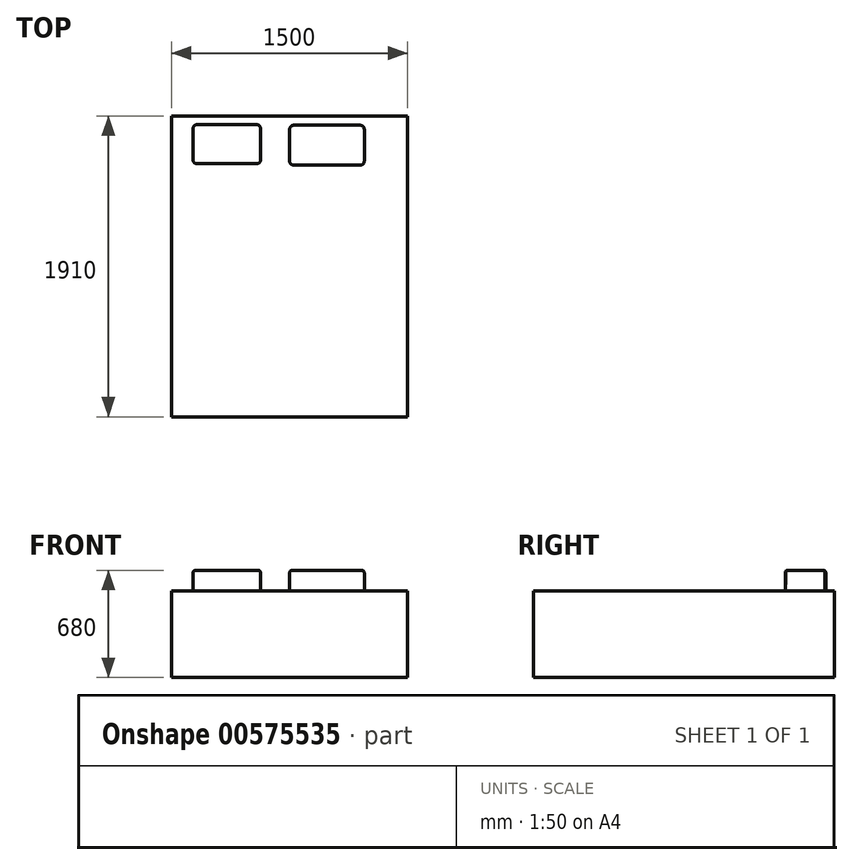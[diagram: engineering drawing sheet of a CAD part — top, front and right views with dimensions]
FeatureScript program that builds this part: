
annotation { "Feature Type Name" : "Feature", "Feature Type Description" : "" }
export const myFeature = defineFeature(function(context is Context, id is Id, definition is map)
    precondition{}
    {
        {
            var Q0;
            Q0=qCreatedBy(makeId("Top.planeOp"),FACE);
            var sketch = newSketch(context, id + "F0", { "sketchPlane" : qUnion([Q0])});
            skLineSegment(sketch, "E0.bottom", {"start": v(0, 0) * mm, "end": v(-1500, 0) * mm});
            skLineSegment(sketch, "E0.top", {"start": v(0, 1910) * mm, "end": v(-1500, 1910) * mm});
            skLineSegment(sketch, "E0.left", {"start": v(0, 0) * mm, "end": v(0, 1910) * mm});
            skLineSegment(sketch, "E0.right", {"start": v(-1500, 0) * mm, "end": v(-1500, 1910) * mm});
            skSolve(sketch);
        }
        {
            var Q0;
            Q0 = qSketchRegion(id + "F0", true);
            extrude(context, id + "F1", {"entities" : qUnion([Q0]), "depth" : 550 * mm, "offsetDistance" : 25 * mm});
        }
        {
            var Q0;
            Q0=makeQuery(id+"F1.opExtrude","CAP_FACE",FACE,{"disambiguationData":[OSD([sQuery(id+"F0.wireOp",EDGE,"E0.bottom"),sQuery(id+"F0.wireOp",EDGE,"E0.top"),sQuery(id+"F0.wireOp",EDGE,"E0.left"),sQuery(id+"F0.wireOp",EDGE,"E0.right")])],"isStart":false});
            var sketch = newSketch(context, id + "F2", { "sketchPlane" : qUnion([Q0])});
            skLineSegment(sketch, "E1.bottom", {"start": v(-1362.1, 1856.2) * mm, "end": v(-933.6, 1856.2) * mm});
            skLineSegment(sketch, "E1.top", {"start": v(-1362.1, 1607.61) * mm, "end": v(-933.6, 1607.61) * mm});
            skLineSegment(sketch, "E1.left", {"start": v(-1362.1, 1856.2) * mm, "end": v(-1362.1, 1607.61) * mm});
            skLineSegment(sketch, "E1.right", {"start": v(-933.6, 1856.2) * mm, "end": v(-933.6, 1607.61) * mm});
            skLineSegment(sketch, "E2.bottom", {"start": v(-748.36, 1851.76) * mm, "end": v(-274.86, 1851.76) * mm});
            skLineSegment(sketch, "E2.top", {"start": v(-748.36, 1598.73) * mm, "end": v(-274.86, 1598.73) * mm});
            skLineSegment(sketch, "E2.left", {"start": v(-748.36, 1851.76) * mm, "end": v(-748.36, 1598.73) * mm});
            skLineSegment(sketch, "E2.right", {"start": v(-274.86, 1851.76) * mm, "end": v(-274.86, 1598.73) * mm});
            skSolve(sketch);
        }
        {
            var Q0;
            Q0 = qSketchRegion(id + "F2", true);
            extrude(context, id + "F3", {"entities" : qUnion([Q0]), "operationType" : NewBodyOperationType.ADD, "depth" : 130 * mm, "offsetDistance" : 25 * mm});
        }
        {
            var Q0;
            Q0=makeQuery(id+"F3.opExtrude","CAP_FACE",FACE,{"disambiguationData":[OSD([sQuery(id+"F2.wireOp",EDGE,"E1.bottom"),sQuery(id+"F2.wireOp",EDGE,"E1.top"),sQuery(id+"F2.wireOp",EDGE,"E1.left"),sQuery(id+"F2.wireOp",EDGE,"E1.right")])],"isStart":false});
            var Q1;
            Q1=makeQuery(id+"F3.opExtrude","CAP_FACE",FACE,{"disambiguationData":[OSD([sQuery(id+"F2.wireOp",EDGE,"E2.bottom"),sQuery(id+"F2.wireOp",EDGE,"E2.top"),sQuery(id+"F2.wireOp",EDGE,"E2.left"),sQuery(id+"F2.wireOp",EDGE,"E2.right")])],"isStart":false});
            fillet(context, id + "F4", {"entities" : qUnion([Q0, Q1]), "radius" : 15 * mm, "tangentPropagation" : true, "allowEdgeOverflow" : false});
        }
        {
            var Q0;
            Q0=makeQuery(id+"F3.opExtrude","SWEPT_EDGE",EDGE,{"disambiguationData":[OSD([sQuery(id+"F2.wireOp",EDGE,"E1.top"),sQuery(id+"F2.wireOp",EDGE,"E1.left")])]});
            var Q1;
            Q1=makeQuery(id+"F3.opExtrude","SWEPT_EDGE",EDGE,{"disambiguationData":[OSD([sQuery(id+"F2.wireOp",EDGE,"E1.top"),sQuery(id+"F2.wireOp",EDGE,"E1.right")])]});
            var Q2;
            Q2=makeQuery(id+"F3.opExtrude","SWEPT_EDGE",EDGE,{"disambiguationData":[OSD([sQuery(id+"F2.wireOp",EDGE,"E2.top"),sQuery(id+"F2.wireOp",EDGE,"E2.left")])]});
            var Q3;
            Q3=makeQuery(id+"F3.opExtrude","SWEPT_EDGE",EDGE,{"disambiguationData":[OSD([sQuery(id+"F2.wireOp",EDGE,"E2.top"),sQuery(id+"F2.wireOp",EDGE,"E2.right")])]});
            var Q4;
            Q4=makeQuery(id+"F3.opExtrude","SWEPT_EDGE",EDGE,{"disambiguationData":[OSD([sQuery(id+"F2.wireOp",EDGE,"E1.bottom"),sQuery(id+"F2.wireOp",EDGE,"E1.right")])]});
            var Q5;
            Q5=makeQuery(id+"F3.opExtrude","SWEPT_EDGE",EDGE,{"disambiguationData":[OSD([sQuery(id+"F2.wireOp",EDGE,"E1.bottom"),sQuery(id+"F2.wireOp",EDGE,"E1.left")])]});
            var Q6;
            Q6=makeQuery(id+"F3.opExtrude","SWEPT_EDGE",EDGE,{"disambiguationData":[OSD([sQuery(id+"F2.wireOp",EDGE,"E2.bottom"),sQuery(id+"F2.wireOp",EDGE,"E2.left")])]});
            var Q7;
            Q7=makeQuery(id+"F3.opExtrude","SWEPT_EDGE",EDGE,{"disambiguationData":[OSD([sQuery(id+"F2.wireOp",EDGE,"E2.bottom"),sQuery(id+"F2.wireOp",EDGE,"E2.right")])]});
            fillet(context, id + "F5", {"entities" : qUnion([Q0, Q1, Q2, Q3, Q4, Q5, Q6, Q7]), "radius" : 25 * mm, "tangentPropagation" : true, "allowEdgeOverflow" : false});
        }
    });
